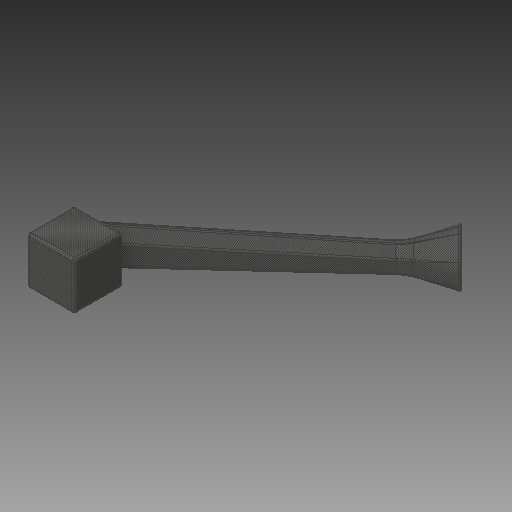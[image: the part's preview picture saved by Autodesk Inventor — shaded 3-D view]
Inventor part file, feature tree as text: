
AUTODESK INVENTOR PART (.ipt)
format: ipt  version: 2018 (Build 220112000, 112)  size: 2,037,760 bytes
history: native  units: in
note: dims shown in document units (in); Inventor stores cm internally (conversion verified against a paired STEP export)
features: sketch x11, plane x5, other x3
ambient origin geometry x8: Origin, YZ Plane, XZ Plane, XY Plane, X Axis, Y Axis, Z Axis, Center Point
bodies: Solid1 (feature_tree)
feature tree (19):
  other  "arm 5,6.ipt"
  other  "Solid1::arm 5,6.ipt"
  other  "TaggingFeature1"
  sketch  "Sketch1"  dims[d0=0.3937in]
  sketch  "Sketch2"
  sketch  "Sketch3"
  sketch  "Sketch8"
  sketch  "Sketch9"
  sketch  "Sketch10"
  sketch  "Sketch11"
  sketch  "Sketch12"
  sketch  "Sketch13"
  sketch  "Sketch14"
  sketch  "Sketch15"
  plane  "Work Plane1"
  plane  "Work Plane2"
  plane  "Work Plane5"
  plane  "Work Plane6"
  plane  "Work Plane7"
